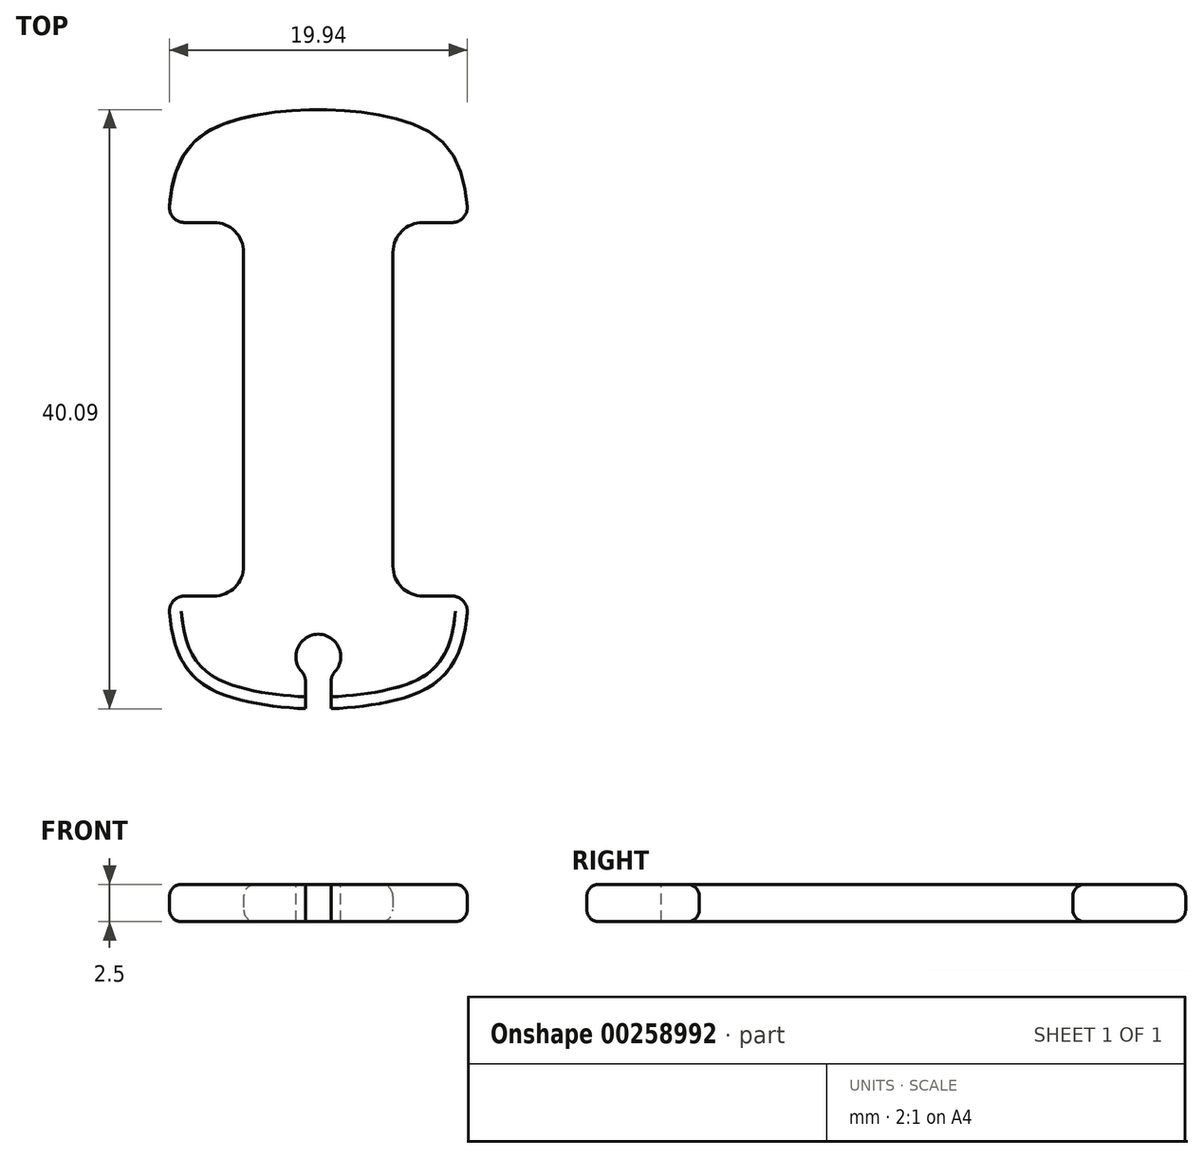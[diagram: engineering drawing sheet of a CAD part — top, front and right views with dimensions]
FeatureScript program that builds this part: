
annotation { "Feature Type Name" : "Feature", "Feature Type Description" : "" }
export const myFeature = defineFeature(function(context is Context, id is Id, definition is map)
    precondition{}
    {
        {
            var Q0;
            Q0=qCreatedBy(makeId("Top.planeOp"),FACE);
            var sketch = newSketch(context, id + "F0", { "sketchPlane" : qUnion([Q0])});
            skLineSegment(sketch, "E0.bottom", {"start": v(-5, 12.5) * mm, "end": v(5, 12.5) * mm, "construction": true});
            skLineSegment(sketch, "E0.top", {"start": v(-5, -12.5) * mm, "end": v(5, -12.5) * mm, "construction": true});
            skLineSegment(sketch, "E0.left", {"start": v(-5, 12.5) * mm, "end": v(-5, -12.5) * mm});
            skLineSegment(sketch, "E0.right", {"start": v(5, 12.5) * mm, "end": v(5, -12.5) * mm});
            skLineSegment(sketch, "E1", {"start": v(-5, 12.5) * mm, "end": v(-10, 12.5) * mm});
            skLineSegment(sketch, "E2", {"start": v(-10, 12.5) * mm, "end": v(-5, 12.5) * mm});
            skLineSegment(sketch, "E3", {"start": v(-10, -12.5) * mm, "end": v(-5, -12.5) * mm});
            skFitSpline(sketch, "E4", {"points": [v(-10, 12.5) * mm, v(-5, 19.5) * mm, v(5, 19.5) * mm, v(10, 12.5) * mm], "startDerivative": vector(0, 46.17) * mm, "endDerivative": vector(0, -46.17) * mm});
            skFitSpline(sketch, "E5", {"points": [v(-10, -12.5) * mm, v(-5, -19.5) * mm, v(5, -19.5) * mm, v(10, -12.5) * mm], "startDerivative": vector(0, -46.17) * mm, "endDerivative": vector(0, 46.17) * mm});
            skLineSegment(sketch, "E6", {"start": v(-5, 29.08) * mm, "end": v(-5, -39.74) * mm, "construction": true});
            skPoint(sketch, "E6.startSnap0", {"position": v(-5, 0) * mm});
            skLineSegment(sketch, "E7", {"start": v(5, 25.13) * mm, "end": v(5, -32.28) * mm, "construction": true});
            skLineSegment(sketch, "E8", {"start": v(-10, 12.5) * mm, "end": v(-10, 28.74) * mm, "construction": true});
            skLineSegment(sketch, "E9", {"start": v(10, 12.5) * mm, "end": v(10, 21.93) * mm, "construction": true});
            skLineSegment(sketch, "E10", {"start": v(-10, -12.5) * mm, "end": v(-10, -34.26) * mm, "construction": true});
            skLineSegment(sketch, "E11", {"start": v(10, -12.5) * mm, "end": v(10, -26.8) * mm, "construction": true});
            skLineSegment(sketch, "E12.trimOffspring", {"start": v(5, 12.5) * mm, "end": v(10, 12.5) * mm});
            skLineSegment(sketch, "E13.trimOffspring", {"start": v(5, -12.5) * mm, "end": v(10, -12.5) * mm});
            skLineSegment(sketch, "E14", {"start": v(-5, 19.5) * mm, "end": v(5, 19.5) * mm, "construction": true});
            skLineSegment(sketch, "E15", {"start": v(-5, -19.5) * mm, "end": v(5, -19.5) * mm, "construction": true});
            skSolve(sketch);
        }
        {
            var Q0;
            Q0 = qSketchRegion(id + "F0", true);
            extrude(context, id + "F1", {"entities" : qUnion([Q0]), "depth" : 2.5 * mm});
        }
        {
            var Q0;
            Q0=makeQuery(id+"F1.opExtrude","SWEPT_EDGE",EDGE,{"disambiguationData":[OSD([sQuery(id+"F0.wireOp",EDGE,"E0.left"),sQuery(id+"F0.wireOp",EDGE,"E2")])]});
            var Q1;
            Q1=makeQuery(id+"F1.opExtrude","SWEPT_EDGE",EDGE,{"disambiguationData":[OSD([sQuery(id+"F0.wireOp",EDGE,"E0.right"),sQuery(id+"F0.wireOp",EDGE,"E12.trimOffspring")])]});
            var Q2;
            Q2=makeQuery(id+"F1.opExtrude","SWEPT_EDGE",EDGE,{"disambiguationData":[OSD([sQuery(id+"F0.wireOp",EDGE,"E0.right"),sQuery(id+"F0.wireOp",EDGE,"E13.trimOffspring")])]});
            var Q3;
            Q3=makeQuery(id+"F1.opExtrude","SWEPT_EDGE",EDGE,{"disambiguationData":[OSD([sQuery(id+"F0.wireOp",EDGE,"E0.left"),sQuery(id+"F0.wireOp",EDGE,"E3")])]});
            fillet(context, id + "F2", {"entities" : qUnion([Q0, Q1, Q2, Q3]), "radius" : 2 * mm, "tangentPropagation" : true, "allowEdgeOverflow" : false});
        }
        {
            var Q0;
            Q0=makeQuery(id+"F1.opExtrude","SWEPT_EDGE",EDGE,{"disambiguationData":[OSD([sQuery(id+"F0.wireOp",EDGE,"E3"),sQuery(id+"F0.wireOp",EDGE,"E5")])]});
            var Q1;
            Q1=makeQuery(id+"F1.opExtrude","SWEPT_EDGE",EDGE,{"disambiguationData":[OSD([sQuery(id+"F0.wireOp",EDGE,"E5"),sQuery(id+"F0.wireOp",EDGE,"E13.trimOffspring")])]});
            var Q2;
            Q2=makeQuery(id+"F1.opExtrude","SWEPT_EDGE",EDGE,{"disambiguationData":[OSD([sQuery(id+"F0.wireOp",EDGE,"E4"),sQuery(id+"F0.wireOp",EDGE,"E12.trimOffspring")])]});
            var Q3;
            Q3=makeQuery(id+"F1.opExtrude","SWEPT_EDGE",EDGE,{"disambiguationData":[OSD([sQuery(id+"F0.wireOp",EDGE,"E2"),sQuery(id+"F0.wireOp",EDGE,"E4")])]});
            fillet(context, id + "F3", {"entities" : qUnion([Q0, Q1, Q2, Q3]), "radius" : 1 * mm, "tangentPropagation" : true, "allowEdgeOverflow" : false});
        }
        {
            var Q0;
            Q0=makeQuery(id+"F1.opExtrude","CAP_FACE",FACE,{"disambiguationData":[OSD([sQuery(id+"F0.wireOp",EDGE,"E0.left"),sQuery(id+"F0.wireOp",EDGE,"E0.right"),sQuery(id+"F0.wireOp",EDGE,"E2"),sQuery(id+"F0.wireOp",EDGE,"E3"),sQuery(id+"F0.wireOp",EDGE,"E4"),sQuery(id+"F0.wireOp",EDGE,"E5"),sQuery(id+"F0.wireOp",EDGE,"E12.trimOffspring"),sQuery(id+"F0.wireOp",EDGE,"E13.trimOffspring")])],"isStart":false});
            var Q1;
            Q1=makeQuery(id+"F1.opExtrude","CAP_FACE",FACE,{"disambiguationData":[OSD([sQuery(id+"F0.wireOp",EDGE,"E0.left"),sQuery(id+"F0.wireOp",EDGE,"E0.right"),sQuery(id+"F0.wireOp",EDGE,"E2"),sQuery(id+"F0.wireOp",EDGE,"E3"),sQuery(id+"F0.wireOp",EDGE,"E4"),sQuery(id+"F0.wireOp",EDGE,"E5"),sQuery(id+"F0.wireOp",EDGE,"E12.trimOffspring"),sQuery(id+"F0.wireOp",EDGE,"E13.trimOffspring")])],"isStart":true});
            fillet(context, id + "F4", {"entities" : qUnion([Q0, Q1]), "radius" : .8 * mm, "tangentPropagation" : true, "allowEdgeOverflow" : false});
        }
        {
            var Q0;
            Q0=makeQuery(id+"F1.opExtrude","CAP_FACE",FACE,{"disambiguationData":[OSD([sQuery(id+"F0.wireOp",EDGE,"E0.left"),sQuery(id+"F0.wireOp",EDGE,"E0.right"),sQuery(id+"F0.wireOp",EDGE,"E2"),sQuery(id+"F0.wireOp",EDGE,"E3"),sQuery(id+"F0.wireOp",EDGE,"E4"),sQuery(id+"F0.wireOp",EDGE,"E5"),sQuery(id+"F0.wireOp",EDGE,"E12.trimOffspring"),sQuery(id+"F0.wireOp",EDGE,"E13.trimOffspring")])],"isStart":false});
            var sketch = newSketch(context, id + "F5", { "sketchPlane" : qUnion([Q0])});
            skCircle(sketch, "E16", {"center": v(0, -16.55) * mm, "radius": 1.5 * mm});
            skLineSegment(sketch, "E17.bottom", {"start": v(-0.86, -17.78) * mm, "end": v(0.86, -17.78) * mm});
            skLineSegment(sketch, "E17.top", {"start": v(-0.86, -24.4) * mm, "end": v(0.86, -24.4) * mm});
            skLineSegment(sketch, "E17.left", {"start": v(-0.86, -17.78) * mm, "end": v(-0.86, -24.4) * mm});
            skLineSegment(sketch, "E17.right", {"start": v(0.86, -17.78) * mm, "end": v(0.86, -24.4) * mm});
            skSolve(sketch);
        }
        {
            var Q0;
            Q0 = qSketchRegion(id + "F5", true);
            extrude(context, id + "F6", {"entities" : qUnion([Q0]), "operationType" : NewBodyOperationType.REMOVE, "endBound" : BoundingType.THROUGH_ALL, "oppositeDirection" : true, "depth" : 25 * mm});
        }
        {
            var Q0;
            Q0=makeQuery(id+"F6.boolean.opBoolean","COPY",EDGE,{"derivedFrom":makeQuery(id+"F6.opExtrude","SWEPT_EDGE",EDGE,{"disambiguationData":[OSD([sQuery(id+"F5.wireOp",EDGE,"E16"),sQuery(id+"F5.wireOp",EDGE,"E17.bottom"),sQuery(id+"F5.wireOp",EDGE,"E17.left")])]})});
            var Q1;
            Q1=makeQuery(id+"F6.boolean.opBoolean","COPY",EDGE,{"derivedFrom":makeQuery(id+"F6.opExtrude","SWEPT_EDGE",EDGE,{"disambiguationData":[OSD([sQuery(id+"F5.wireOp",EDGE,"E16"),sQuery(id+"F5.wireOp",EDGE,"E17.bottom"),sQuery(id+"F5.wireOp",EDGE,"E17.right")])]})});
            fillet(context, id + "F7", {"entities" : qUnion([Q0, Q1]), "radius" : 1 * mm, "tangentPropagation" : true, "allowEdgeOverflow" : false});
        }
    });
